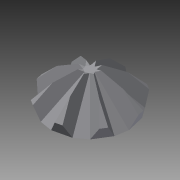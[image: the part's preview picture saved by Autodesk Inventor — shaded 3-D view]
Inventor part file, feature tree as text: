
AUTODESK INVENTOR PART (.ipt)
format: ipt  version: 2015 (Build 190159000, 159)  size: 141,312 bytes
history: native  units: in
note: dims shown in document units (in); Inventor stores cm internally (conversion verified against a paired STEP export)
features: extrude x3, sketch x3, pattern_circular x2, chamfer x1
ambient origin geometry x8: Origin, YZ Plane, XZ Plane, XY Plane, X Axis, Y Axis, Z Axis, Center Point
bodies: Body1 (feature_tree)
feature tree (9):
  extrude  "Extrusion6"  TaperAngle=45.0deg  [1 undecoded]
  chamfer  "Chamfer2"  Distance=0.75in
  pattern_circular  "Circular Pattern3"  Count=8 Angle=360.0deg
  extrude  "Extrusion7"  Depth=0.1in
  extrude  "Extrusion8"  Depth=0.1in TaperAngle=0.0deg
  pattern_circular  "Circular Pattern4"  Count=8 Angle=360.0deg
  sketch  "Sketch7"  dims[d25=0.875in d26=45.0deg d27=0.75in d28=0.0in]
  sketch  "Sketch8"  dims[d29=0.75in d30=0.125in d31=45.0deg d32=3.1496in d33=360.0deg]
  sketch  "Sketch9"  dims[d35=0.25in d36=-0.1622in d37=0.375in d38=0.1in d39=0.0in d40=3.1496in d41=360.0deg]
note: 1 required parameter value undecoded (feature->parameter linkage not recoverable at this tier; creation-order binding heuristic only, values carry confidence <= 0.55)
